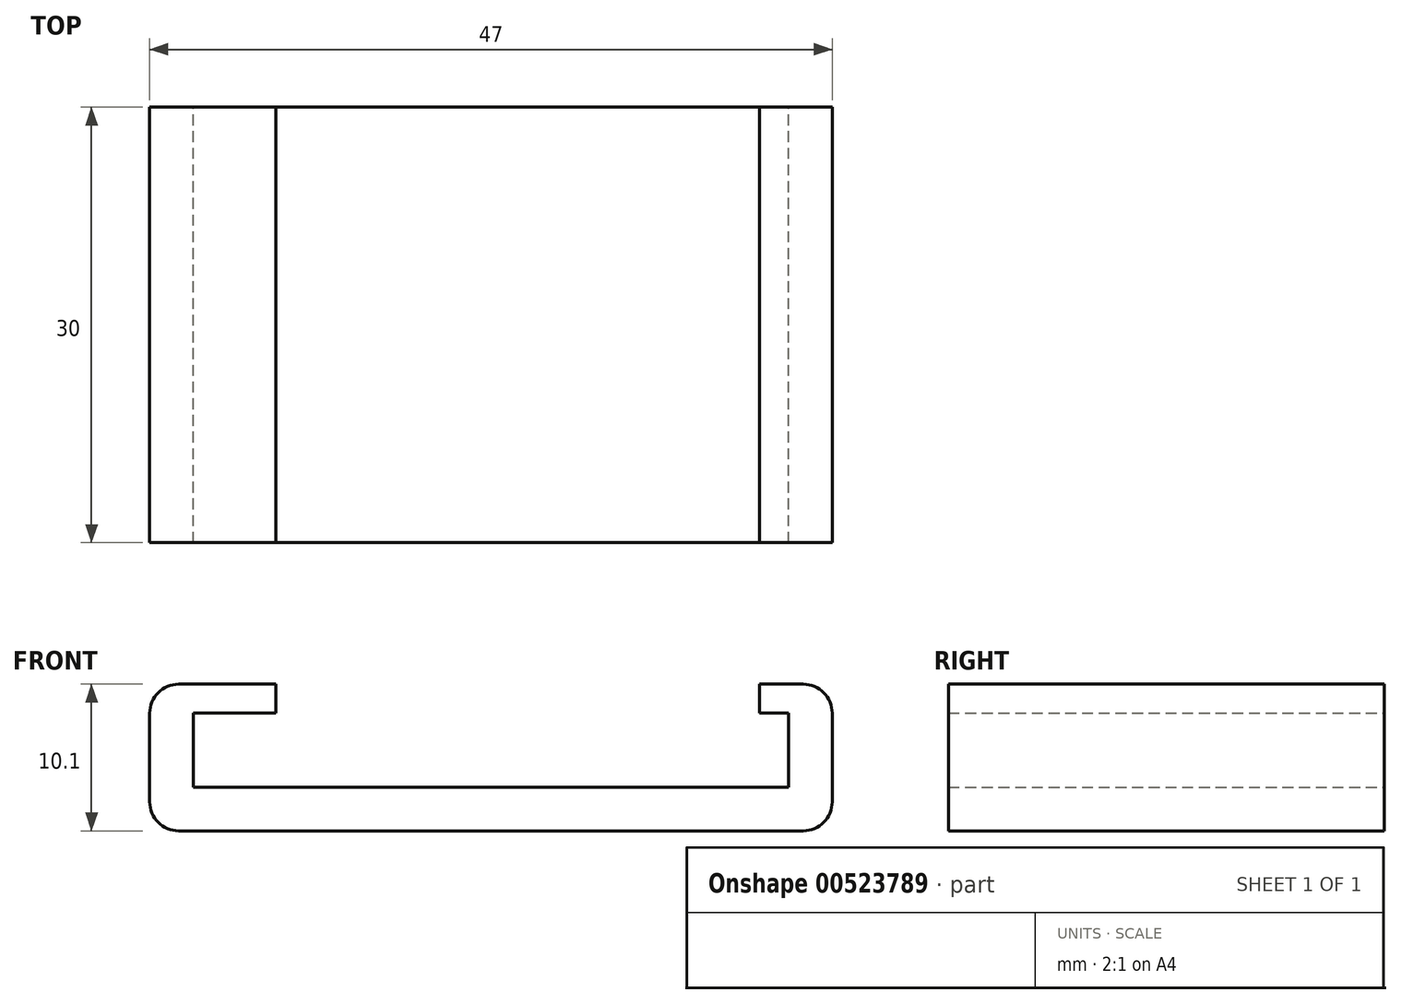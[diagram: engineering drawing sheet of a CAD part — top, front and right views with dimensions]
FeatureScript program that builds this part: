
annotation { "Feature Type Name" : "Feature", "Feature Type Description" : "" }
export const myFeature = defineFeature(function(context is Context, id is Id, definition is map)
    precondition{}
    {
        {
            var Q0;
            Q0=qCreatedBy(makeId("Front.planeOp"),FACE);
            var sketch = newSketch(context, id + "F0", { "sketchPlane" : qUnion([Q0])});
            skLineSegment(sketch, "E0.bottom", {"start": v(0, 0) * mm, "end": v(-23, 0) * mm});
            skLineSegment(sketch, "E0.top", {"start": v(0, 3) * mm, "end": v(-20, 3) * mm});
            skLineSegment(sketch, "E1", {"start": v(-23, 10.1) * mm, "end": v(-14.3, 10.1) * mm});
            skLineSegment(sketch, "E2", {"start": v(-14.3, 10.1) * mm, "end": v(-14.3, 8.1) * mm});
            skLineSegment(sketch, "E3", {"start": v(-14.3, 8.1) * mm, "end": v(-20, 8.1) * mm});
            skLineSegment(sketch, "E4", {"start": v(-20, 8.1) * mm, "end": v(-20, 3) * mm});
            skLineSegment(sketch, "E5", {"start": v(-23, 10.1) * mm, "end": v(-23, 0) * mm});
            skLineSegment(sketch, "E6.MirrorCS", {"start": v(0, 3) * mm, "end": v(21, 3) * mm});
            skLineSegment(sketch, "E7.MirrorCS", {"start": v(0, 0) * mm, "end": v(24, 0) * mm});
            skLineSegment(sketch, "E8.MirrorCS", {"start": v(21, 8.1) * mm, "end": v(21, 3) * mm});
            skLineSegment(sketch, "E9.MirrorCS", {"start": v(24, 10.1) * mm, "end": v(24, 0) * mm});
            skLineSegment(sketch, "E10.MirrorCS", {"start": v(24, 10.1) * mm, "end": v(19, 10.1) * mm});
            skLineSegment(sketch, "E11.MirrorCS", {"start": v(19, 8.1) * mm, "end": v(21, 8.1) * mm});
            skLineSegment(sketch, "E12.MirrorCS", {"start": v(19, 10.1) * mm, "end": v(19, 8.1) * mm});
            skSolve(sketch);
        }
        {
            var Q0;
            Q0=makeQuery(id+"F0.imprint","IMPRINT",FACE,{"disambiguationData":[TD([[makeQuery(id+"F0.imprint","IMPRINT",EDGE,{"derivedFrom":sQuery(id+"F0.wireOp",EDGE,"E0.bottom")}),-1.0]])]});
            extrude(context, id + "F1", {"entities" : qUnion([Q0]), "depth" : 30 * mm, "offsetDistance" : 25 * mm});
        }
        {
            var Q0;
            Q0=makeQuery(id+"F1.opExtrude","SWEPT_EDGE",EDGE,{"disambiguationData":[OSD([sQuery(id+"F0.wireOp",EDGE,"E1"),sQuery(id+"F0.wireOp",EDGE,"E5")])]});
            var Q1;
            Q1=makeQuery(id+"F1.opExtrude","SWEPT_EDGE",EDGE,{"disambiguationData":[OSD([sQuery(id+"F0.wireOp",EDGE,"E9.MirrorCS"),sQuery(id+"F0.wireOp",EDGE,"E10.MirrorCS")])]});
            var Q2;
            Q2=makeQuery(id+"F1.opExtrude","SWEPT_EDGE",EDGE,{"disambiguationData":[OSD([sQuery(id+"F0.wireOp",EDGE,"E0.bottom"),sQuery(id+"F0.wireOp",EDGE,"E5")])]});
            var Q3;
            Q3=makeQuery(id+"F1.opExtrude","SWEPT_EDGE",EDGE,{"disambiguationData":[OSD([sQuery(id+"F0.wireOp",EDGE,"E7.MirrorCS"),sQuery(id+"F0.wireOp",EDGE,"E9.MirrorCS")])]});
            fillet(context, id + "F2", {"entities" : qUnion([Q0, Q1, Q2, Q3]), "radius" : 2 * mm, "tangentPropagation" : true, "allowEdgeOverflow" : false});
        }
    });
